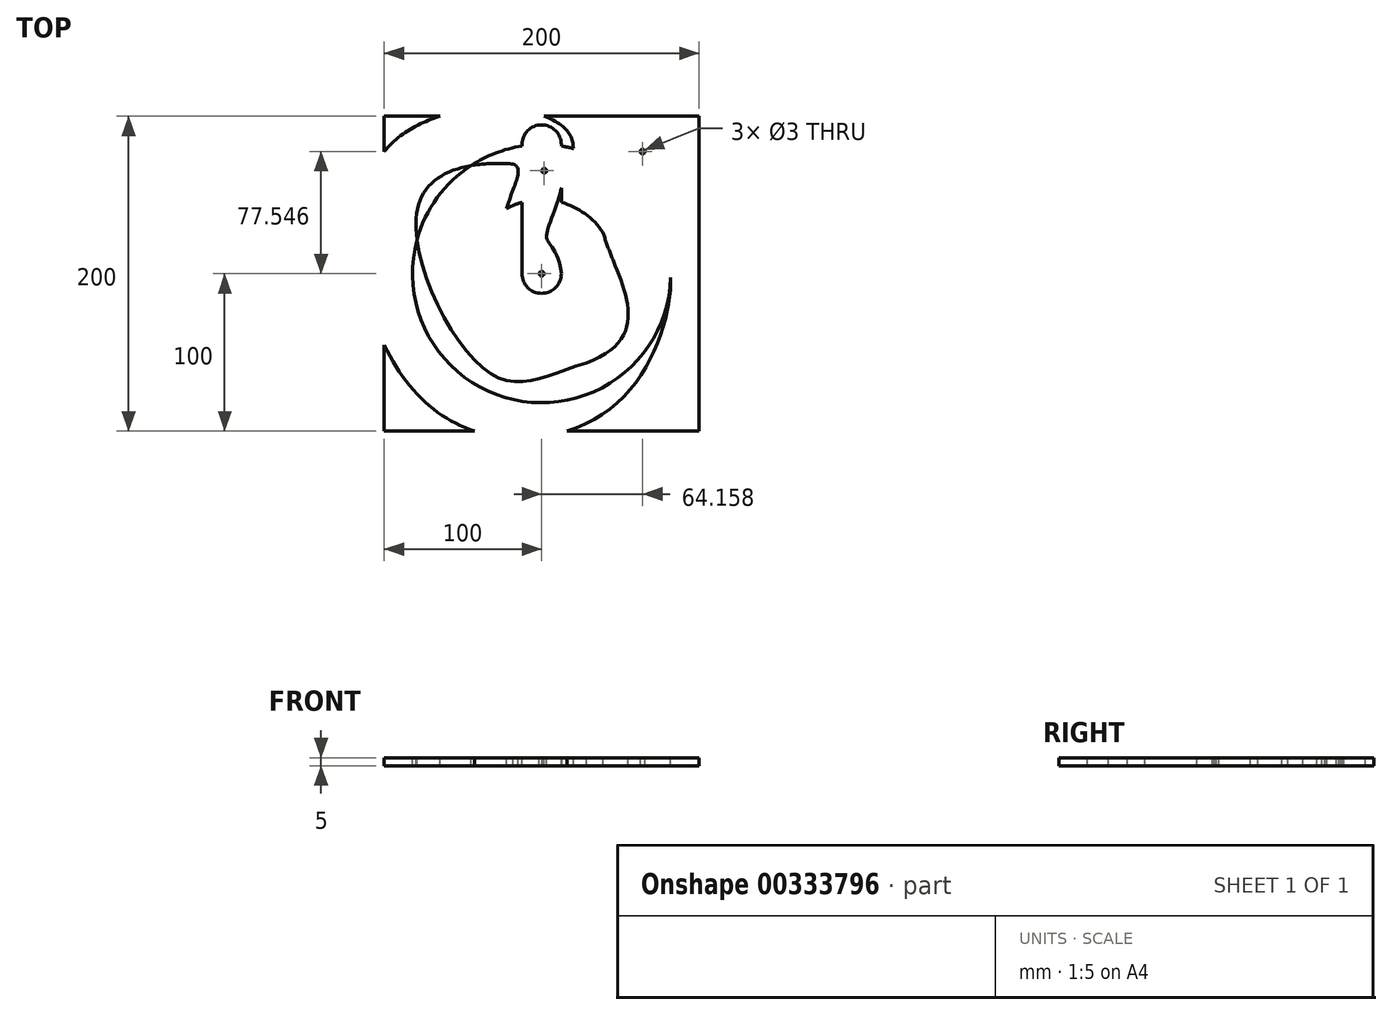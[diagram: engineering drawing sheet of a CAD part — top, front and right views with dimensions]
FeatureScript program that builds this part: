
annotation { "Feature Type Name" : "Feature", "Feature Type Description" : "" }
export const myFeature = defineFeature(function(context is Context, id is Id, definition is map)
    precondition{}
    {
        {
            var Q0;
            Q0=qCreatedBy(makeId("Top.planeOp"),FACE);
            var sketch = newSketch(context, id + "F0", { "sketchPlane" : qUnion([Q0])});
            skLineSegment(sketch, "E0.bottom", {"start": v(100, 100) * mm, "end": v(-100, 100) * mm});
            skLineSegment(sketch, "E0.top", {"start": v(100, -100) * mm, "end": v(-100, -100) * mm});
            skLineSegment(sketch, "E0.left", {"start": v(100, 100) * mm, "end": v(100, -100) * mm});
            skLineSegment(sketch, "E0.right", {"start": v(-100, 100) * mm, "end": v(-100, -100) * mm});
            skPoint(sketch, "E0.middle", {"position": v(0, 0) * mm});
            skSolve(sketch);
        }
        {
            var Q0;
            Q0=qSketchRegion(id+"F0",true);
            extrude(context, id + "F1", {"entities" : qUnion([Q0]), "depth" : 5 * mm});
        }
        {
            var Q0;
            Q0=makeQuery(id+"F1.opExtrude","CAP_FACE",FACE,{"disambiguationData":[OSD([sQuery(id+"F0.wireOp",EDGE,"E0.bottom"),sQuery(id+"F0.wireOp",EDGE,"E0.top"),sQuery(id+"F0.wireOp",EDGE,"E0.left"),sQuery(id+"F0.wireOp",EDGE,"E0.right")])],"isStart":false});
            var sketch = newSketch(context, id + "F2", { "sketchPlane" : qUnion([Q0])});
            skCircle(sketch, "E1", {"center": v(0, 0) * mm, "radius": 1.5 * mm});
            skCircle(sketch, "E2", {"center": v(0, -63.66) * mm, "radius": 1.5 * mm});
            skCircle(sketch, "E3", {"center": v(64.16, 77.55) * mm, "radius": 1.5 * mm});
            skCircle(sketch, "E4", {"center": v(-51.92, 31.01) * mm, "radius": 1.5 * mm});
            skCircle(sketch, "E5", {"center": v(1.67, 65.37) * mm, "radius": 1.5 * mm});
            skSolve(sketch);
        }
        {
            var Q0;
            Q0=qSketchRegion(id+"F2",true);
            extrude(context, id + "F3", {"entities" : qUnion([Q0]), "operationType" : NewBodyOperationType.REMOVE, "endBound" : BoundingType.THROUGH_ALL, "oppositeDirection" : true, "depth" : 25 * mm});
        }
        {
            var Q0;
            Q0=makeQuery(id+"F1.opExtrude","CAP_FACE",FACE,{"disambiguationData":[OSD([sQuery(id+"F0.wireOp",EDGE,"E0.bottom"),sQuery(id+"F0.wireOp",EDGE,"E0.top"),sQuery(id+"F0.wireOp",EDGE,"E0.left"),sQuery(id+"F0.wireOp",EDGE,"E0.right")])],"isStart":false});
            var sketch = newSketch(context, id + "F4", { "sketchPlane" : qUnion([Q0])});
            skCircle(sketch, "E6", {"center": v(0, 0) * mm, "radius": 82 * mm});
            skCircle(sketch, "E7", {"center": v(0, 0) * mm, "radius": 47 * mm});
            skLineSegment(sketch, "E8", {"start": v(0, 0) * mm, "end": v(0, 82) * mm});
            skArc(sketch, "E9.0.startCap", {"start": v(12.5, 0) * mm, "mid": v(0, -12.5) * mm, "end": v(-12.5, 0) * mm});
            skArc(sketch, "E9.0.endCap", {"start": v(-12.5, 82) * mm, "mid": v(0, 94.5) * mm, "end": v(12.5, 82) * mm});
            skLineSegment(sketch, "E9.0.left", {"start": v(-12.5, 0) * mm, "end": v(-12.5, 82) * mm});
            skLineSegment(sketch, "E9.0.right", {"start": v(12.5, 0) * mm, "end": v(12.5, 82) * mm});
            skFitSpline(sketch, "E10", {"points": [v(12.5, 0) * mm, v(3.26, 22.84) * mm, v(12.5, 54.43) * mm], "startDerivative": vector(-11.7, 100.36) * mm, "endDerivative": vector(19.92, 92.42) * mm});
            skFitSpline(sketch, "E11", {"points": [v(-18.02, 69.66) * mm, v(-23.82, 32.52) * mm, v(5.3, -11.32) * mm], "startDerivative": vector(59.25, -24.3) * mm, "endDerivative": vector(98.56, 35.83) * mm});
            skFitSpline(sketch, "E12", {"points": [v(28.42, -56.6) * mm, v(-32.09, -63.63) * mm, v(-78.47, 42.8) * mm, v(-18.02, 69.66) * mm], "startDerivative": vector(-250.8, -77.17) * mm, "endDerivative": vector(274.04, -20.1) * mm});
            skFitSpline(sketch, "E13", {"points": [v(12.5, 54.43) * mm, v(18.09, 87.96) * mm, v(-96.04, 82) * mm, v(-72.23, -83.04) * mm, v(47, -82.93) * mm, v(81.96, -2.54) * mm], "startDerivative": vector(27.67, 108.77) * mm, "endDerivative": vector(-8.28, 329.13) * mm});
            skFitSpline(sketch, "E14", {"points": [v(28.42, -56.6) * mm, v(39.08, 26.12) * mm, v(45.16, 77.4) * mm, v(57.9, 93.04) * mm, v(84.1, 87.25) * mm, v(72.53, 50.74) * mm, v(81.96, -2.54) * mm], "startDerivative": vector(616.52, 223.53) * mm, "endDerivative": vector(-35.18, -523.4) * mm});
            skSolve(sketch);
        }
        {
            var Q0;
            {var subQ0=sQuery(id+"F4.wireOp",EDGE,"53124a5a-5f37-4aa6-af82-e1a15b688f27");Q0=makeQuery(id+"F4.imprint","IMPRINT",FACE,{"disambiguationData":[TD([[makeQuery(id+"F4.imprint","IMPRINT",EDGE,{"derivedFrom":subQ0}),-1.0]])]});}
            var Q1;
            {var subQ5=sQuery(id+"F4.wireOp",EDGE,"740dab77-b675-45c8-9115-fba3ba689b44");Q1=makeQuery(id+"F4.imprint","IMPRINT",FACE,{"disambiguationData":[TD([[makeQuery(id+"F4.imprint","IMPRINT",EDGE,{"derivedFrom":subQ5}),1.0]])]});}
            var Q2;
            {var subQ1=sQuery(id+"F4.wireOp",EDGE,"E7");var subQ4=sQuery(id+"F4.wireOp",EDGE,"E9.0.left");var subQ9=makeQuery(id+"F4.imprint","INTERSECT",VERTEX,{"derivedFrom":[subQ1,subQ4]});Q2=makeQuery(id+"F4.imprint","IMPRINT",FACE,{"disambiguationData":[TD([[makeQuery(id+"F4.imprint","IMPRINT",EDGE,{"disambiguationData":[TD([[subQ9,-1.0]])],"derivedFrom":subQ1}),1.0]])]});}
            var Q3;
            {var subQ0=sQuery(id+"F4.wireOp",EDGE,"E11");var subQ1=sQuery(id+"F4.wireOp",EDGE,"E7");var subQ2=makeQuery(id+"F4.imprint","INTERSECT",VERTEX,{"derivedFrom":[subQ1,subQ0]});Q3=makeQuery(id+"F4.imprint","IMPRINT",FACE,{"disambiguationData":[TD([[makeQuery(id+"F4.imprint","IMPRINT",EDGE,{"disambiguationData":[TD([[subQ2,-1.0]])],"derivedFrom":subQ1}),-1.0]])]});}
            var Q4;
            {var subQ0=sQuery(id+"F4.wireOp",EDGE,"E11");var subQ1=sQuery(id+"F4.wireOp",EDGE,"E7");var subQ2=makeQuery(id+"F4.imprint","INTERSECT",VERTEX,{"derivedFrom":[subQ1,subQ0]});Q4=makeQuery(id+"F4.imprint","IMPRINT",FACE,{"disambiguationData":[TD([[makeQuery(id+"F4.imprint","IMPRINT",EDGE,{"disambiguationData":[TD([[subQ2,-1.0]])],"derivedFrom":subQ1}),1.0]])]});}
            var Q5;
            {var subQ0=sQuery(id+"F4.wireOp",EDGE,"E10");var subQ1=sQuery(id+"F4.wireOp",EDGE,"E7");var subQ2=makeQuery(id+"F4.imprint","INTERSECT",VERTEX,{"derivedFrom":[subQ1,subQ0]});Q5=makeQuery(id+"F4.imprint","IMPRINT",FACE,{"disambiguationData":[TD([[makeQuery(id+"F4.imprint","IMPRINT",EDGE,{"disambiguationData":[TD([[subQ2,1.0]])],"derivedFrom":subQ1}),1.0]])]});}
            var Q6;
            {var subQ0=sQuery(id+"F4.wireOp",EDGE,"E10");var subQ1=sQuery(id+"F4.wireOp",EDGE,"E7");var subQ2=makeQuery(id+"F4.imprint","INTERSECT",VERTEX,{"derivedFrom":[subQ1,subQ0]});Q6=makeQuery(id+"F4.imprint","IMPRINT",FACE,{"disambiguationData":[TD([[makeQuery(id+"F4.imprint","IMPRINT",EDGE,{"disambiguationData":[TD([[subQ2,1.0]])],"derivedFrom":subQ1}),-1.0]])]});}
            var Q7;
            {var subQ0=sQuery(id+"F4.wireOp",EDGE,"E9.0.left");var subQ1=sQuery(id+"F4.wireOp",EDGE,"E9.0.endCap");var subQ2=makeQuery(id+"F4.imprint","INTERSECT",VERTEX,{"derivedFrom":[subQ1,subQ0]});Q7=makeQuery(id+"F4.imprint","IMPRINT",FACE,{"disambiguationData":[TD([[makeQuery(id+"F4.imprint","IMPRINT",EDGE,{"disambiguationData":[TD([[subQ2,-1.0]])],"derivedFrom":subQ1}),-1.0]])]});}
            var Q8;
            {var subQ0=sQuery(id+"F4.wireOp",EDGE,"6028a9ff-b76b-4c52-9491-26ae1ed70332");var subQ3=sQuery(id+"F4.wireOp",EDGE,"E6");var subQ4=makeQuery(id+"F4.imprint","INTERSECT",VERTEX,{"disambiguationData":[OD(1.0)],"derivedFrom":[subQ3,subQ0]});Q8=makeQuery(id+"F4.imprint","IMPRINT",FACE,{"disambiguationData":[TD([[makeQuery(id+"F4.imprint","IMPRINT",EDGE,{"disambiguationData":[TD([[subQ4,1.0]])],"derivedFrom":subQ3}),1.0]])]});}
            extrude(context, id + "F5", {"entities" : qUnion([Q0, Q1, Q2, Q3, Q4, Q5, Q6, Q7, Q8]), "operationType" : NewBodyOperationType.REMOVE, "endBound" : BoundingType.THROUGH_ALL, "oppositeDirection" : true, "depth" : 25 * mm});
        }
    });
